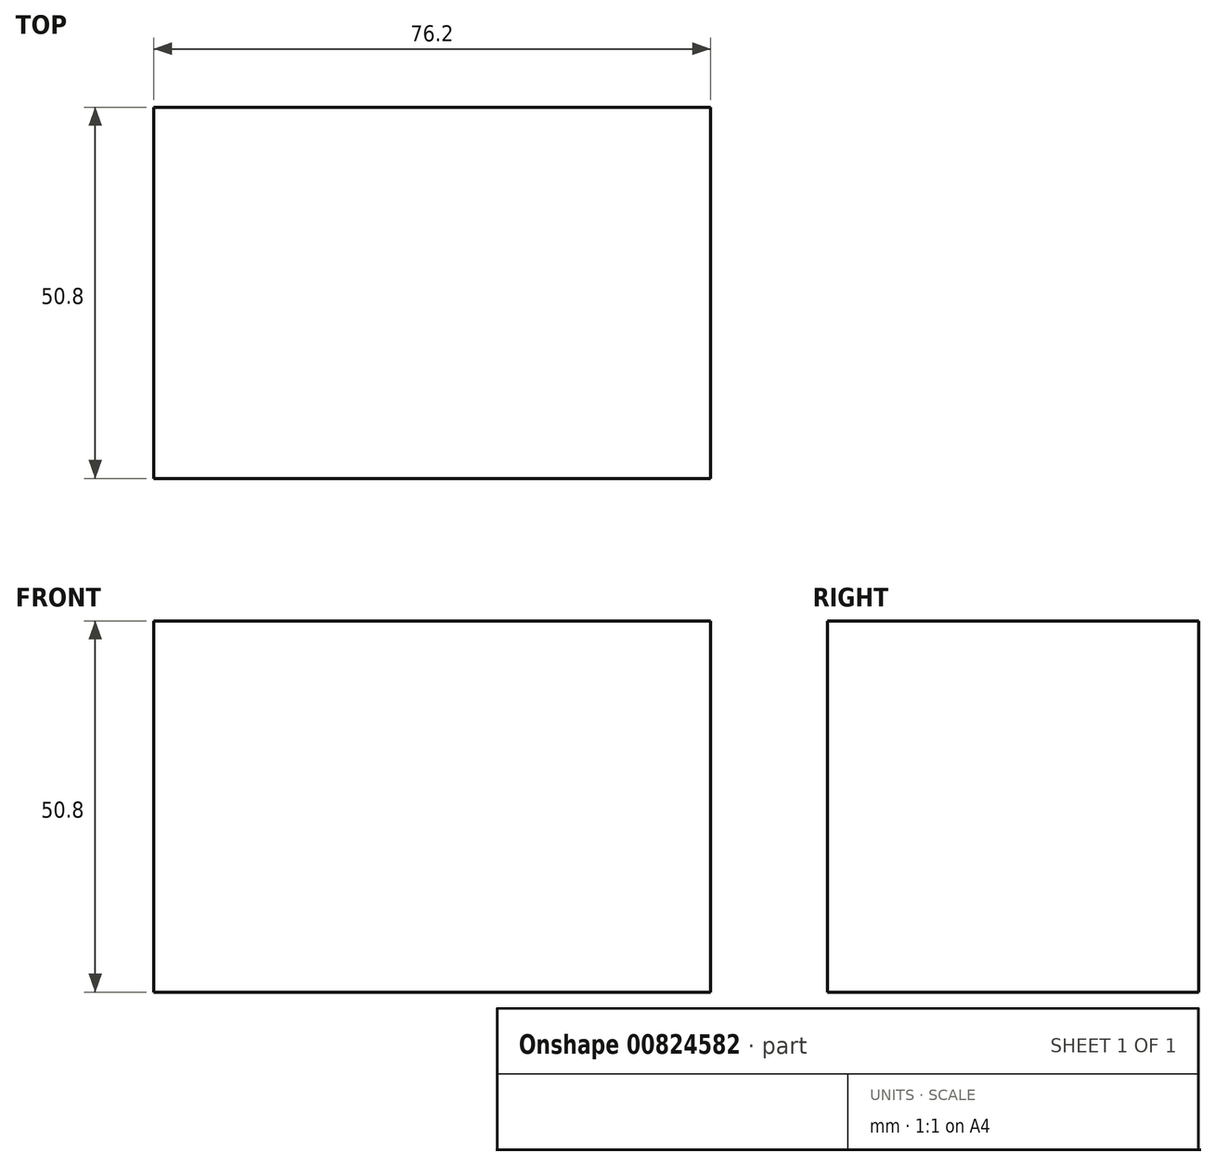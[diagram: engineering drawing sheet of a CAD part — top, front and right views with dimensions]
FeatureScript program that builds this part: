
annotation { "Feature Type Name" : "Feature", "Feature Type Description" : "" }
export const myFeature = defineFeature(function(context is Context, id is Id, definition is map)
    precondition{}
    {
        {
            var Q0;
            Q0=qCreatedBy(makeId("Top.planeOp"),FACE);
            var sketch = newSketch(context, id + "F0", { "sketchPlane" : qUnion([Q0])});
            skLineSegment(sketch, "E0", {"start": v(0, 0) * mm, "end": v(76.2, 0) * mm});
            skLineSegment(sketch, "E1", {"start": v(76.2, 0) * mm, "end": v(76.2, 50.8) * mm});
            skLineSegment(sketch, "E2", {"start": v(76.2, 50.8) * mm, "end": v(0, 50.8) * mm});
            skLineSegment(sketch, "E3", {"start": v(0, 50.8) * mm, "end": v(0, 0) * mm});
            skSolve(sketch);
        }
        {
            var Q0;
            Q0=makeQuery(id+"F0.imprint","IMPRINT",FACE,{"disambiguationData":[TD([[makeQuery(id+"F0.imprint","IMPRINT",EDGE,{"derivedFrom":sQuery(id+"F0.wireOp",EDGE,"E0")}),1.0]])]});
            extrude(context, id + "F1", {"entities" : qUnion([Q0]), "depth" : 50.8 * mm, "offsetDistance" : 25.4 * mm});
        }
    });
